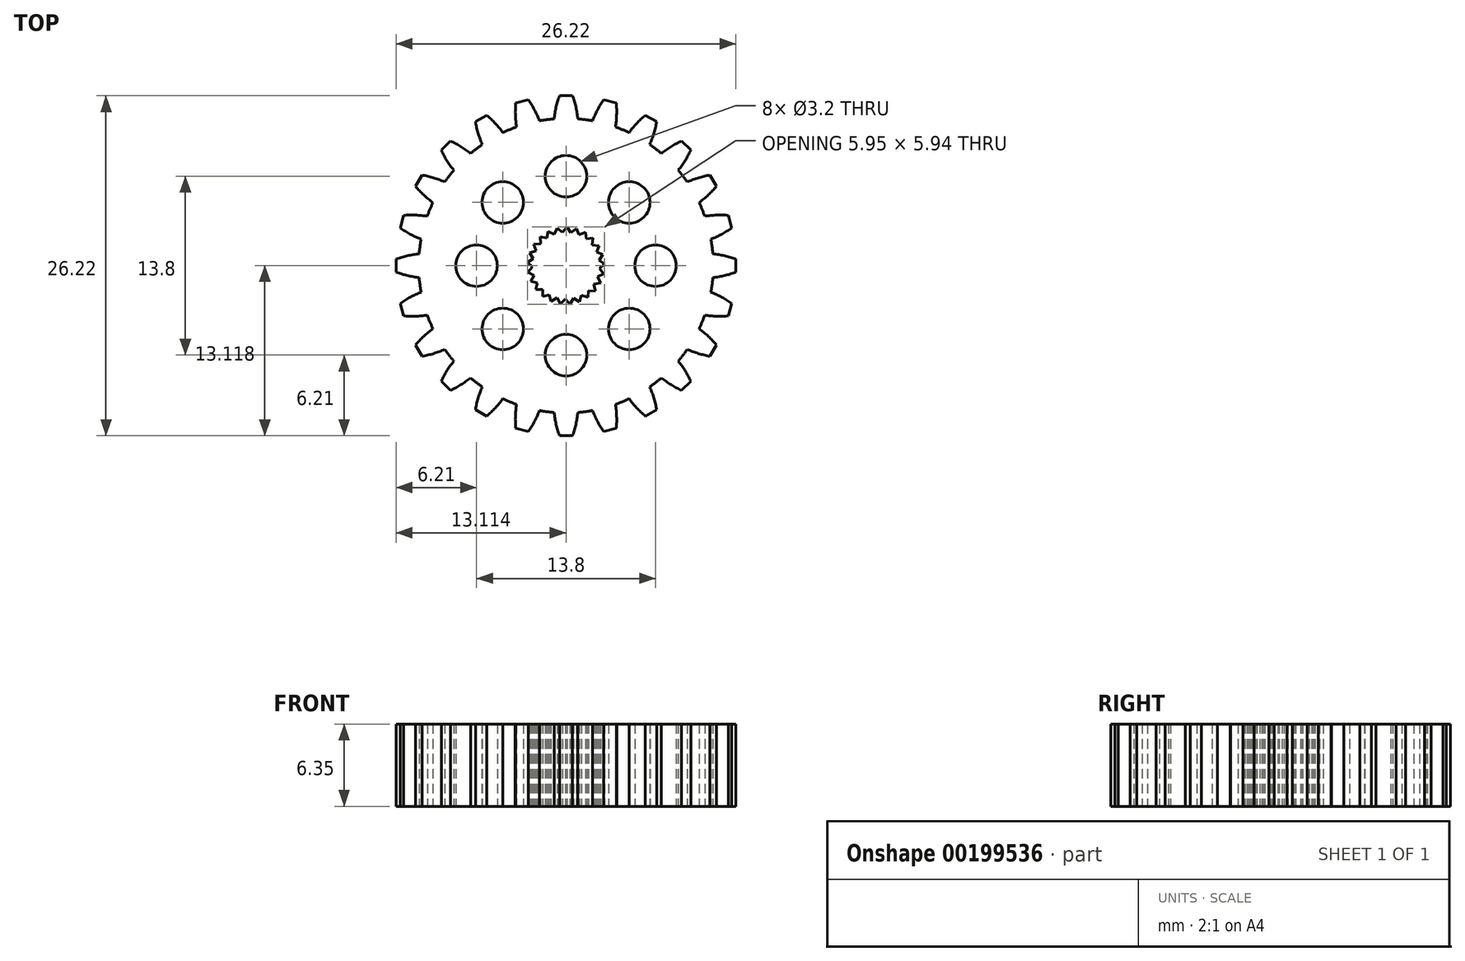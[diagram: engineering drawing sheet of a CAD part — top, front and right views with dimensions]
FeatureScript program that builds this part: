
annotation { "Feature Type Name" : "Feature", "Feature Type Description" : "" }
export const myFeature = defineFeature(function(context is Context, id is Id, definition is map)
    precondition{}
    {
        {
            var Q0;
            Q0=qCreatedBy(makeId("Top.planeOp"),FACE);
            var sketch = newSketch(context, id + "F0", { "sketchPlane" : qUnion([Q0])});
            skLineSegment(sketch, "E0", {"start": v(-0.5, 13.1) * mm, "end": v(0.5, 13.1) * mm});
            skArc(sketch, "E1", {"start": v(-0.5, 13.1) * mm, "mid": v(-0.76, 12.23) * mm, "end": v(-0.91, 11.32) * mm});
            skArc(sketch, "E2.MirrorCS", {"start": v(0.5, 13.1) * mm, "mid": v(0.76, 12.23) * mm, "end": v(0.91, 11.32) * mm});
            skPoint(sketch, "E3.center", {"position": v(0, 0) * mm});
            skLineSegment(sketch, "E4", {"start": v(-2.48, 1.65) * mm, "end": v(-2.31, 1.15) * mm});
            skLineSegment(sketch, "E5", {"start": v(-2.31, 1.15) * mm, "end": v(-2.81, 0.98) * mm});
            skLineSegment(sketch, "E6.1.0", {"start": v(-2.81, 0.98) * mm, "end": v(-2.53, 0.54) * mm});
            skLineSegment(sketch, "E6.1.1", {"start": v(-2.53, 0.54) * mm, "end": v(-2.97, 0.25) * mm});
            skLineSegment(sketch, "E6.2.0", {"start": v(-2.97, 0.25) * mm, "end": v(-2.58, -0.1) * mm});
            skLineSegment(sketch, "E6.2.1", {"start": v(-2.58, -0.1) * mm, "end": v(-2.94, -0.5) * mm});
            skLineSegment(sketch, "E6.3.0", {"start": v(-2.94, -0.5) * mm, "end": v(-2.47, -0.74) * mm});
            skLineSegment(sketch, "E6.3.1", {"start": v(-2.47, -0.74) * mm, "end": v(-2.72, -1.2) * mm});
            skLineSegment(sketch, "E6.4.0", {"start": v(-2.72, -1.2) * mm, "end": v(-2.21, -1.34) * mm});
            skLineSegment(sketch, "E6.4.1", {"start": v(-2.21, -1.34) * mm, "end": v(-2.34, -1.85) * mm});
            skLineSegment(sketch, "E6.5.0", {"start": v(-2.34, -1.85) * mm, "end": v(-1.8, -1.84) * mm});
            skLineSegment(sketch, "E6.5.1", {"start": v(-1.8, -1.84) * mm, "end": v(-1.8, -2.37) * mm});
            skLineSegment(sketch, "E6.6.0", {"start": v(-1.8, -2.37) * mm, "end": v(-1.3, -2.24) * mm});
            skLineSegment(sketch, "E6.6.1", {"start": v(-1.3, -2.24) * mm, "end": v(-1.16, -2.75) * mm});
            skLineSegment(sketch, "E6.7.0", {"start": v(-1.16, -2.75) * mm, "end": v(-0.7, -2.49) * mm});
            skLineSegment(sketch, "E6.7.1", {"start": v(-0.7, -2.49) * mm, "end": v(-0.44, -2.95) * mm});
            skLineSegment(sketch, "E6.8.0", {"start": v(-0.44, -2.95) * mm, "end": v(-0.06, -2.58) * mm});
            skLineSegment(sketch, "E6.8.1", {"start": v(-0.06, -2.58) * mm, "end": v(0.3, -2.96) * mm});
            skLineSegment(sketch, "E6.9.0", {"start": v(0.3, -2.96) * mm, "end": v(0.59, -2.52) * mm});
            skLineSegment(sketch, "E6.9.1", {"start": v(0.59, -2.52) * mm, "end": v(1.04, -2.8) * mm});
            skLineSegment(sketch, "E6.10.0", {"start": v(1.04, -2.8) * mm, "end": v(1.2, -2.3) * mm});
            skLineSegment(sketch, "E6.10.1", {"start": v(1.2, -2.3) * mm, "end": v(1.7, -2.45) * mm});
            skLineSegment(sketch, "E6.11.0", {"start": v(1.7, -2.45) * mm, "end": v(1.73, -1.92) * mm});
            skLineSegment(sketch, "E6.11.1", {"start": v(1.73, -1.92) * mm, "end": v(2.25, -1.95) * mm});
            skLineSegment(sketch, "E6.12.0", {"start": v(2.25, -1.95) * mm, "end": v(2.15, -1.43) * mm});
            skLineSegment(sketch, "E6.12.1", {"start": v(2.15, -1.43) * mm, "end": v(2.67, -1.33) * mm});
            skLineSegment(sketch, "E6.13.0", {"start": v(2.67, -1.33) * mm, "end": v(2.44, -0.85) * mm});
            skLineSegment(sketch, "E6.13.1", {"start": v(2.44, -0.85) * mm, "end": v(2.91, -0.62) * mm});
            skLineSegment(sketch, "E6.14.0", {"start": v(2.91, -0.62) * mm, "end": v(2.57, -0.22) * mm});
            skLineSegment(sketch, "E6.14.1", {"start": v(2.57, -0.22) * mm, "end": v(2.98, 0.12) * mm});
            skLineSegment(sketch, "E6.15.0", {"start": v(2.98, 0.12) * mm, "end": v(2.55, 0.43) * mm});
            skLineSegment(sketch, "E6.15.1", {"start": v(2.55, 0.43) * mm, "end": v(2.85, 0.86) * mm});
            skLineSegment(sketch, "E6.16.0", {"start": v(2.85, 0.86) * mm, "end": v(2.36, 1.05) * mm});
            skLineSegment(sketch, "E6.16.1", {"start": v(2.36, 1.05) * mm, "end": v(2.55, 1.54) * mm});
            skLineSegment(sketch, "E6.17.0", {"start": v(2.55, 1.54) * mm, "end": v(2.03, 1.6) * mm});
            skLineSegment(sketch, "E6.17.1", {"start": v(2.03, 1.6) * mm, "end": v(2.09, 2.13) * mm});
            skLineSegment(sketch, "E6.18.0", {"start": v(2.09, 2.13) * mm, "end": v(1.56, 2.06) * mm});
            skLineSegment(sketch, "E6.18.1", {"start": v(1.56, 2.06) * mm, "end": v(1.5, 2.58) * mm});
            skLineSegment(sketch, "E6.19.0", {"start": v(1.5, 2.58) * mm, "end": v(1, 2.38) * mm});
            skLineSegment(sketch, "E6.19.1", {"start": v(1, 2.38) * mm, "end": v(0.8, 2.87) * mm});
            skLineSegment(sketch, "E6.20.0", {"start": v(0.8, 2.87) * mm, "end": v(0.38, 2.56) * mm});
            skLineSegment(sketch, "E6.20.1", {"start": v(0.38, 2.56) * mm, "end": v(0.07, 2.98) * mm});
            skLineSegment(sketch, "E6.21.0", {"start": v(0.07, 2.98) * mm, "end": v(-0.27, 2.57) * mm});
            skLineSegment(sketch, "E6.21.1", {"start": v(-0.27, 2.57) * mm, "end": v(-0.68, 2.9) * mm});
            skLineSegment(sketch, "E6.22.0", {"start": v(-0.68, 2.9) * mm, "end": v(-0.9, 2.42) * mm});
            skLineSegment(sketch, "E6.22.1", {"start": v(-0.9, 2.42) * mm, "end": v(-1.38, 2.64) * mm});
            skLineSegment(sketch, "E6.23.0", {"start": v(-1.38, 2.64) * mm, "end": v(-1.47, 2.12) * mm});
            skLineSegment(sketch, "E6.23.1", {"start": v(-1.47, 2.12) * mm, "end": v(-2, 2.22) * mm});
            skLineSegment(sketch, "E6.24.0", {"start": v(-2, 2.22) * mm, "end": v(-1.95, 1.69) * mm});
            skLineSegment(sketch, "E6.24.1", {"start": v(-1.95, 1.69) * mm, "end": v(-2.48, 1.65) * mm});
            skCircle(sketch, "E7", {"center": v(0, 6.9) * mm, "radius": 1.6 * mm});
            skCircle(sketch, "E8.1.0", {"center": v(-4.88, 4.88) * mm, "radius": 1.6 * mm});
            skCircle(sketch, "E8.2.0", {"center": v(-6.9, 0) * mm, "radius": 1.6 * mm});
            skCircle(sketch, "E8.3.0", {"center": v(-4.88, -4.88) * mm, "radius": 1.6 * mm});
            skCircle(sketch, "E8.4.0", {"center": v(0, -6.9) * mm, "radius": 1.6 * mm});
            skCircle(sketch, "E8.5.0", {"center": v(4.88, -4.88) * mm, "radius": 1.6 * mm});
            skCircle(sketch, "E8.6.0", {"center": v(6.9, 0) * mm, "radius": 1.6 * mm});
            skCircle(sketch, "E8.7.0", {"center": v(4.88, 4.88) * mm, "radius": 1.6 * mm});
            skPoint(sketch, "E9.1.4", {"position": v(-0.5, 13.1) * mm});
            skArc(sketch, "E10", {"start": v(2.05, 11.18) * mm, "mid": v(1.48, 11.26) * mm, "end": v(0.91, 11.32) * mm});
            skPoint(sketch, "E11.orphan", {"position": v(2.9, 12.8) * mm});
            skPoint(sketch, "E12.orphan", {"position": v(0.94, 11) * mm});
            skPoint(sketch, "E13.orphan", {"position": v(-0.94, 11) * mm});
            skPoint(sketch, "E14.orphan", {"position": v(-2.9, 12.8) * mm});
            skArc(sketch, "E15.1.0", {"start": v(-0.91, 11.32) * mm, "mid": v(-1.48, 11.26) * mm, "end": v(-2.05, 11.18) * mm});
            skPoint(sketch, "E15.1.1", {"position": v(-3.88, 12.53) * mm});
            skArc(sketch, "E15.1.2", {"start": v(-3.88, 12.53) * mm, "mid": v(-3.9, 11.61) * mm, "end": v(-3.81, 10.7) * mm});
            skPoint(sketch, "E15.1.3", {"position": v(-3.75, 10.38) * mm});
            skArc(sketch, "E15.1.5", {"start": v(-2.9, 12.8) * mm, "mid": v(-2.43, 12.01) * mm, "end": v(-2.05, 11.18) * mm});
            skLineSegment(sketch, "E15.1.6", {"start": v(-3.88, 12.53) * mm, "end": v(-2.9, 12.8) * mm});
            skPoint(sketch, "E15.1.7", {"position": v(-1.94, 10.87) * mm});
            skArc(sketch, "E15.2.0", {"start": v(-3.81, 10.7) * mm, "mid": v(-4.35, 10.5) * mm, "end": v(-4.87, 10.26) * mm});
            skPoint(sketch, "E15.2.1", {"position": v(-6.99, 11.1) * mm});
            skArc(sketch, "E15.2.2", {"start": v(-6.99, 11.1) * mm, "mid": v(-6.78, 10.2) * mm, "end": v(-6.45, 9.35) * mm});
            skPoint(sketch, "E15.2.3", {"position": v(-6.31, 9.06) * mm});
            skPoint(sketch, "E15.2.4", {"position": v(-3.88, 12.53) * mm});
            skArc(sketch, "E15.2.5", {"start": v(-6.12, 11.6) * mm, "mid": v(-5.45, 10.97) * mm, "end": v(-4.87, 10.26) * mm});
            skLineSegment(sketch, "E15.2.6", {"start": v(-6.99, 11.1) * mm, "end": v(-6.12, 11.6) * mm});
            skPoint(sketch, "E15.2.7", {"position": v(-4.69, 10) * mm});
            skArc(sketch, "E15.3.0", {"start": v(-6.45, 9.35) * mm, "mid": v(-6.92, 9.01) * mm, "end": v(-7.36, 8.65) * mm});
            skPoint(sketch, "E15.3.1", {"position": v(-9.62, 8.91) * mm});
            skArc(sketch, "E15.3.2", {"start": v(-9.62, 8.91) * mm, "mid": v(-9.19, 8.1) * mm, "end": v(-8.65, 7.36) * mm});
            skPoint(sketch, "E15.3.3", {"position": v(-8.44, 7.11) * mm});
            skPoint(sketch, "E15.3.4", {"position": v(-6.99, 11.1) * mm});
            skArc(sketch, "E15.3.5", {"start": v(-8.91, 9.62) * mm, "mid": v(-8.1, 9.19) * mm, "end": v(-7.36, 8.65) * mm});
            skLineSegment(sketch, "E15.3.6", {"start": v(-9.62, 8.91) * mm, "end": v(-8.91, 9.62) * mm});
            skPoint(sketch, "E15.3.7", {"position": v(-7.11, 8.44) * mm});
            skArc(sketch, "E15.4.0", {"start": v(-8.65, 7.36) * mm, "mid": v(-9.01, 6.92) * mm, "end": v(-9.35, 6.45) * mm});
            skPoint(sketch, "E15.4.1", {"position": v(-11.6, 6.12) * mm});
            skArc(sketch, "E15.4.2", {"start": v(-11.6, 6.12) * mm, "mid": v(-10.97, 5.45) * mm, "end": v(-10.26, 4.87) * mm});
            skPoint(sketch, "E15.4.3", {"position": v(-10, 4.69) * mm});
            skPoint(sketch, "E15.4.4", {"position": v(-9.62, 8.91) * mm});
            skArc(sketch, "E15.4.5", {"start": v(-11.1, 6.99) * mm, "mid": v(-10.2, 6.78) * mm, "end": v(-9.35, 6.45) * mm});
            skLineSegment(sketch, "E15.4.6", {"start": v(-11.6, 6.12) * mm, "end": v(-11.1, 6.99) * mm});
            skPoint(sketch, "E15.4.7", {"position": v(-9.06, 6.31) * mm});
            skArc(sketch, "E15.5.0", {"start": v(-10.26, 4.87) * mm, "mid": v(-10.5, 4.35) * mm, "end": v(-10.7, 3.81) * mm});
            skPoint(sketch, "E15.5.1", {"position": v(-12.8, 2.9) * mm});
            skArc(sketch, "E15.5.2", {"start": v(-12.8, 2.9) * mm, "mid": v(-12.01, 2.43) * mm, "end": v(-11.18, 2.05) * mm});
            skPoint(sketch, "E15.5.3", {"position": v(-10.87, 1.94) * mm});
            skPoint(sketch, "E15.5.4", {"position": v(-11.6, 6.12) * mm});
            skArc(sketch, "E15.5.5", {"start": v(-12.53, 3.88) * mm, "mid": v(-11.61, 3.9) * mm, "end": v(-10.7, 3.81) * mm});
            skLineSegment(sketch, "E15.5.6", {"start": v(-12.8, 2.9) * mm, "end": v(-12.53, 3.88) * mm});
            skPoint(sketch, "E15.5.7", {"position": v(-10.38, 3.75) * mm});
            skArc(sketch, "E15.6.0", {"start": v(-11.18, 2.05) * mm, "mid": v(-11.26, 1.48) * mm, "end": v(-11.32, 0.91) * mm});
            skPoint(sketch, "E15.6.1", {"position": v(-13.1, -0.5) * mm});
            skArc(sketch, "E15.6.2", {"start": v(-13.1, -0.5) * mm, "mid": v(-12.23, -0.76) * mm, "end": v(-11.32, -0.91) * mm});
            skPoint(sketch, "E15.6.3", {"position": v(-11, -0.94) * mm});
            skPoint(sketch, "E15.6.4", {"position": v(-12.8, 2.9) * mm});
            skArc(sketch, "E15.6.5", {"start": v(-13.1, 0.5) * mm, "mid": v(-12.23, 0.76) * mm, "end": v(-11.32, 0.91) * mm});
            skLineSegment(sketch, "E15.6.6", {"start": v(-13.1, -0.5) * mm, "end": v(-13.1, 0.5) * mm});
            skPoint(sketch, "E15.6.7", {"position": v(-11, 0.94) * mm});
            skArc(sketch, "E15.7.0", {"start": v(-11.32, -0.91) * mm, "mid": v(-11.26, -1.48) * mm, "end": v(-11.18, -2.05) * mm});
            skPoint(sketch, "E15.7.1", {"position": v(-12.53, -3.88) * mm});
            skArc(sketch, "E15.7.2", {"start": v(-12.53, -3.88) * mm, "mid": v(-11.61, -3.9) * mm, "end": v(-10.7, -3.81) * mm});
            skPoint(sketch, "E15.7.3", {"position": v(-10.38, -3.75) * mm});
            skPoint(sketch, "E15.7.4", {"position": v(-13.1, -0.5) * mm});
            skArc(sketch, "E15.7.5", {"start": v(-12.8, -2.9) * mm, "mid": v(-12.01, -2.43) * mm, "end": v(-11.18, -2.05) * mm});
            skLineSegment(sketch, "E15.7.6", {"start": v(-12.53, -3.88) * mm, "end": v(-12.8, -2.9) * mm});
            skPoint(sketch, "E15.7.7", {"position": v(-10.87, -1.94) * mm});
            skArc(sketch, "E15.8.0", {"start": v(-10.7, -3.81) * mm, "mid": v(-10.5, -4.35) * mm, "end": v(-10.26, -4.87) * mm});
            skPoint(sketch, "E15.8.1", {"position": v(-11.1, -6.99) * mm});
            skArc(sketch, "E15.8.2", {"start": v(-11.1, -6.99) * mm, "mid": v(-10.2, -6.78) * mm, "end": v(-9.35, -6.45) * mm});
            skPoint(sketch, "E15.8.3", {"position": v(-9.06, -6.31) * mm});
            skPoint(sketch, "E15.8.4", {"position": v(-12.53, -3.88) * mm});
            skArc(sketch, "E15.8.5", {"start": v(-11.6, -6.12) * mm, "mid": v(-10.97, -5.45) * mm, "end": v(-10.26, -4.87) * mm});
            skLineSegment(sketch, "E15.8.6", {"start": v(-11.1, -6.99) * mm, "end": v(-11.6, -6.12) * mm});
            skPoint(sketch, "E15.8.7", {"position": v(-10, -4.69) * mm});
            skArc(sketch, "E15.9.0", {"start": v(-9.35, -6.45) * mm, "mid": v(-9.01, -6.92) * mm, "end": v(-8.65, -7.36) * mm});
            skPoint(sketch, "E15.9.1", {"position": v(-8.91, -9.62) * mm});
            skArc(sketch, "E15.9.2", {"start": v(-8.91, -9.62) * mm, "mid": v(-8.1, -9.19) * mm, "end": v(-7.36, -8.65) * mm});
            skPoint(sketch, "E15.9.3", {"position": v(-7.11, -8.44) * mm});
            skPoint(sketch, "E15.9.4", {"position": v(-11.1, -6.99) * mm});
            skArc(sketch, "E15.9.5", {"start": v(-9.62, -8.91) * mm, "mid": v(-9.19, -8.1) * mm, "end": v(-8.65, -7.36) * mm});
            skLineSegment(sketch, "E15.9.6", {"start": v(-8.91, -9.62) * mm, "end": v(-9.62, -8.91) * mm});
            skPoint(sketch, "E15.9.7", {"position": v(-8.44, -7.11) * mm});
            skArc(sketch, "E15.10.0", {"start": v(-7.36, -8.65) * mm, "mid": v(-6.92, -9.01) * mm, "end": v(-6.45, -9.35) * mm});
            skPoint(sketch, "E15.10.1", {"position": v(-6.12, -11.6) * mm});
            skArc(sketch, "E15.10.2", {"start": v(-6.12, -11.6) * mm, "mid": v(-5.45, -10.97) * mm, "end": v(-4.87, -10.26) * mm});
            skPoint(sketch, "E15.10.3", {"position": v(-4.69, -10) * mm});
            skPoint(sketch, "E15.10.4", {"position": v(-8.91, -9.62) * mm});
            skArc(sketch, "E15.10.5", {"start": v(-6.99, -11.1) * mm, "mid": v(-6.78, -10.2) * mm, "end": v(-6.45, -9.35) * mm});
            skLineSegment(sketch, "E15.10.6", {"start": v(-6.12, -11.6) * mm, "end": v(-6.99, -11.1) * mm});
            skPoint(sketch, "E15.10.7", {"position": v(-6.31, -9.06) * mm});
            skArc(sketch, "E15.11.0", {"start": v(-4.87, -10.26) * mm, "mid": v(-4.35, -10.5) * mm, "end": v(-3.81, -10.7) * mm});
            skPoint(sketch, "E15.11.1", {"position": v(-2.9, -12.8) * mm});
            skArc(sketch, "E15.11.2", {"start": v(-2.9, -12.8) * mm, "mid": v(-2.43, -12.01) * mm, "end": v(-2.05, -11.18) * mm});
            skPoint(sketch, "E15.11.3", {"position": v(-1.94, -10.87) * mm});
            skPoint(sketch, "E15.11.4", {"position": v(-6.12, -11.6) * mm});
            skArc(sketch, "E15.11.5", {"start": v(-3.88, -12.53) * mm, "mid": v(-3.9, -11.61) * mm, "end": v(-3.81, -10.7) * mm});
            skLineSegment(sketch, "E15.11.6", {"start": v(-2.9, -12.8) * mm, "end": v(-3.88, -12.53) * mm});
            skPoint(sketch, "E15.11.7", {"position": v(-3.75, -10.38) * mm});
            skArc(sketch, "E15.12.0", {"start": v(-2.05, -11.18) * mm, "mid": v(-1.48, -11.26) * mm, "end": v(-0.91, -11.32) * mm});
            skPoint(sketch, "E15.12.1", {"position": v(0.5, -13.1) * mm});
            skArc(sketch, "E15.12.2", {"start": v(0.5, -13.1) * mm, "mid": v(0.76, -12.23) * mm, "end": v(0.91, -11.32) * mm});
            skPoint(sketch, "E15.12.3", {"position": v(0.94, -11) * mm});
            skPoint(sketch, "E15.12.4", {"position": v(-2.9, -12.8) * mm});
            skArc(sketch, "E15.12.5", {"start": v(-0.5, -13.1) * mm, "mid": v(-0.76, -12.23) * mm, "end": v(-0.91, -11.32) * mm});
            skLineSegment(sketch, "E15.12.6", {"start": v(0.5, -13.1) * mm, "end": v(-0.5, -13.1) * mm});
            skPoint(sketch, "E15.12.7", {"position": v(-0.94, -11) * mm});
            skArc(sketch, "E15.13.0", {"start": v(0.91, -11.32) * mm, "mid": v(1.48, -11.26) * mm, "end": v(2.05, -11.18) * mm});
            skPoint(sketch, "E15.13.1", {"position": v(3.88, -12.53) * mm});
            skArc(sketch, "E15.13.2", {"start": v(3.88, -12.53) * mm, "mid": v(3.9, -11.61) * mm, "end": v(3.81, -10.7) * mm});
            skPoint(sketch, "E15.13.3", {"position": v(3.75, -10.38) * mm});
            skPoint(sketch, "E15.13.4", {"position": v(0.5, -13.1) * mm});
            skArc(sketch, "E15.13.5", {"start": v(2.9, -12.8) * mm, "mid": v(2.43, -12.01) * mm, "end": v(2.05, -11.18) * mm});
            skLineSegment(sketch, "E15.13.6", {"start": v(3.88, -12.53) * mm, "end": v(2.9, -12.8) * mm});
            skPoint(sketch, "E15.13.7", {"position": v(1.94, -10.87) * mm});
            skArc(sketch, "E15.14.0", {"start": v(3.81, -10.7) * mm, "mid": v(4.35, -10.5) * mm, "end": v(4.87, -10.26) * mm});
            skPoint(sketch, "E15.14.1", {"position": v(6.99, -11.1) * mm});
            skArc(sketch, "E15.14.2", {"start": v(6.99, -11.1) * mm, "mid": v(6.78, -10.2) * mm, "end": v(6.45, -9.35) * mm});
            skPoint(sketch, "E15.14.3", {"position": v(6.31, -9.06) * mm});
            skPoint(sketch, "E15.14.4", {"position": v(3.88, -12.53) * mm});
            skArc(sketch, "E15.14.5", {"start": v(6.12, -11.6) * mm, "mid": v(5.45, -10.97) * mm, "end": v(4.87, -10.26) * mm});
            skLineSegment(sketch, "E15.14.6", {"start": v(6.99, -11.1) * mm, "end": v(6.12, -11.6) * mm});
            skPoint(sketch, "E15.14.7", {"position": v(4.69, -10) * mm});
            skArc(sketch, "E15.15.0", {"start": v(6.45, -9.35) * mm, "mid": v(6.92, -9.01) * mm, "end": v(7.36, -8.65) * mm});
            skPoint(sketch, "E15.15.1", {"position": v(9.62, -8.91) * mm});
            skArc(sketch, "E15.15.2", {"start": v(9.62, -8.91) * mm, "mid": v(9.19, -8.1) * mm, "end": v(8.65, -7.36) * mm});
            skPoint(sketch, "E15.15.3", {"position": v(8.44, -7.11) * mm});
            skPoint(sketch, "E15.15.4", {"position": v(6.99, -11.1) * mm});
            skArc(sketch, "E15.15.5", {"start": v(8.91, -9.62) * mm, "mid": v(8.1, -9.19) * mm, "end": v(7.36, -8.65) * mm});
            skLineSegment(sketch, "E15.15.6", {"start": v(9.62, -8.91) * mm, "end": v(8.91, -9.62) * mm});
            skPoint(sketch, "E15.15.7", {"position": v(7.11, -8.44) * mm});
            skArc(sketch, "E15.16.0", {"start": v(8.65, -7.36) * mm, "mid": v(9.01, -6.92) * mm, "end": v(9.35, -6.45) * mm});
            skPoint(sketch, "E15.16.1", {"position": v(11.6, -6.12) * mm});
            skArc(sketch, "E15.16.2", {"start": v(11.6, -6.12) * mm, "mid": v(10.97, -5.45) * mm, "end": v(10.26, -4.87) * mm});
            skPoint(sketch, "E15.16.3", {"position": v(10, -4.69) * mm});
            skPoint(sketch, "E15.16.4", {"position": v(9.62, -8.91) * mm});
            skArc(sketch, "E15.16.5", {"start": v(11.1, -6.99) * mm, "mid": v(10.2, -6.78) * mm, "end": v(9.35, -6.45) * mm});
            skLineSegment(sketch, "E15.16.6", {"start": v(11.6, -6.12) * mm, "end": v(11.1, -6.99) * mm});
            skPoint(sketch, "E15.16.7", {"position": v(9.06, -6.31) * mm});
            skArc(sketch, "E15.17.0", {"start": v(10.26, -4.87) * mm, "mid": v(10.5, -4.35) * mm, "end": v(10.7, -3.81) * mm});
            skPoint(sketch, "E15.17.1", {"position": v(12.8, -2.9) * mm});
            skArc(sketch, "E15.17.2", {"start": v(12.8, -2.9) * mm, "mid": v(12.01, -2.43) * mm, "end": v(11.18, -2.05) * mm});
            skPoint(sketch, "E15.17.3", {"position": v(10.87, -1.94) * mm});
            skPoint(sketch, "E15.17.4", {"position": v(11.6, -6.12) * mm});
            skArc(sketch, "E15.17.5", {"start": v(12.53, -3.88) * mm, "mid": v(11.61, -3.9) * mm, "end": v(10.7, -3.81) * mm});
            skLineSegment(sketch, "E15.17.6", {"start": v(12.8, -2.9) * mm, "end": v(12.53, -3.88) * mm});
            skPoint(sketch, "E15.17.7", {"position": v(10.38, -3.75) * mm});
            skArc(sketch, "E15.18.0", {"start": v(11.18, -2.05) * mm, "mid": v(11.26, -1.48) * mm, "end": v(11.32, -0.91) * mm});
            skPoint(sketch, "E15.18.1", {"position": v(13.1, 0.5) * mm});
            skArc(sketch, "E15.18.2", {"start": v(13.1, 0.5) * mm, "mid": v(12.23, 0.76) * mm, "end": v(11.32, 0.91) * mm});
            skPoint(sketch, "E15.18.3", {"position": v(11, 0.94) * mm});
            skPoint(sketch, "E15.18.4", {"position": v(12.8, -2.9) * mm});
            skArc(sketch, "E15.18.5", {"start": v(13.1, -0.5) * mm, "mid": v(12.23, -0.76) * mm, "end": v(11.32, -0.91) * mm});
            skLineSegment(sketch, "E15.18.6", {"start": v(13.1, 0.5) * mm, "end": v(13.1, -0.5) * mm});
            skPoint(sketch, "E15.18.7", {"position": v(11, -0.94) * mm});
            skArc(sketch, "E15.19.0", {"start": v(11.32, 0.91) * mm, "mid": v(11.26, 1.48) * mm, "end": v(11.18, 2.05) * mm});
            skPoint(sketch, "E15.19.1", {"position": v(12.53, 3.88) * mm});
            skArc(sketch, "E15.19.2", {"start": v(12.53, 3.88) * mm, "mid": v(11.61, 3.9) * mm, "end": v(10.7, 3.81) * mm});
            skPoint(sketch, "E15.19.3", {"position": v(10.38, 3.75) * mm});
            skPoint(sketch, "E15.19.4", {"position": v(13.1, 0.5) * mm});
            skArc(sketch, "E15.19.5", {"start": v(12.8, 2.9) * mm, "mid": v(12.01, 2.43) * mm, "end": v(11.18, 2.05) * mm});
            skLineSegment(sketch, "E15.19.6", {"start": v(12.53, 3.88) * mm, "end": v(12.8, 2.9) * mm});
            skPoint(sketch, "E15.19.7", {"position": v(10.87, 1.94) * mm});
            skArc(sketch, "E15.20.0", {"start": v(10.7, 3.81) * mm, "mid": v(10.5, 4.35) * mm, "end": v(10.26, 4.87) * mm});
            skPoint(sketch, "E15.20.1", {"position": v(11.1, 6.99) * mm});
            skArc(sketch, "E15.20.2", {"start": v(11.1, 6.99) * mm, "mid": v(10.2, 6.78) * mm, "end": v(9.35, 6.45) * mm});
            skPoint(sketch, "E15.20.3", {"position": v(9.06, 6.31) * mm});
            skPoint(sketch, "E15.20.4", {"position": v(12.53, 3.88) * mm});
            skArc(sketch, "E15.20.5", {"start": v(11.6, 6.12) * mm, "mid": v(10.97, 5.45) * mm, "end": v(10.26, 4.87) * mm});
            skLineSegment(sketch, "E15.20.6", {"start": v(11.1, 6.99) * mm, "end": v(11.6, 6.12) * mm});
            skPoint(sketch, "E15.20.7", {"position": v(10, 4.69) * mm});
            skArc(sketch, "E15.21.0", {"start": v(9.35, 6.45) * mm, "mid": v(9.01, 6.92) * mm, "end": v(8.65, 7.36) * mm});
            skPoint(sketch, "E15.21.1", {"position": v(8.91, 9.62) * mm});
            skArc(sketch, "E15.21.2", {"start": v(8.91, 9.62) * mm, "mid": v(8.1, 9.19) * mm, "end": v(7.36, 8.65) * mm});
            skPoint(sketch, "E15.21.3", {"position": v(7.11, 8.44) * mm});
            skPoint(sketch, "E15.21.4", {"position": v(11.1, 6.99) * mm});
            skArc(sketch, "E15.21.5", {"start": v(9.62, 8.91) * mm, "mid": v(9.19, 8.1) * mm, "end": v(8.65, 7.36) * mm});
            skLineSegment(sketch, "E15.21.6", {"start": v(8.91, 9.62) * mm, "end": v(9.62, 8.91) * mm});
            skPoint(sketch, "E15.21.7", {"position": v(8.44, 7.11) * mm});
            skArc(sketch, "E15.22.0", {"start": v(7.36, 8.65) * mm, "mid": v(6.92, 9.01) * mm, "end": v(6.45, 9.35) * mm});
            skPoint(sketch, "E15.22.1", {"position": v(6.12, 11.6) * mm});
            skArc(sketch, "E15.22.2", {"start": v(6.12, 11.6) * mm, "mid": v(5.45, 10.97) * mm, "end": v(4.87, 10.26) * mm});
            skPoint(sketch, "E15.22.3", {"position": v(4.69, 10) * mm});
            skPoint(sketch, "E15.22.4", {"position": v(8.91, 9.62) * mm});
            skArc(sketch, "E15.22.5", {"start": v(6.99, 11.1) * mm, "mid": v(6.78, 10.2) * mm, "end": v(6.45, 9.35) * mm});
            skLineSegment(sketch, "E15.22.6", {"start": v(6.12, 11.6) * mm, "end": v(6.99, 11.1) * mm});
            skPoint(sketch, "E15.22.7", {"position": v(6.31, 9.06) * mm});
            skArc(sketch, "E15.23.0", {"start": v(4.87, 10.26) * mm, "mid": v(4.35, 10.5) * mm, "end": v(3.81, 10.7) * mm});
            skArc(sketch, "E15.23.2", {"start": v(2.9, 12.8) * mm, "mid": v(2.43, 12.01) * mm, "end": v(2.05, 11.18) * mm});
            skPoint(sketch, "E15.23.3", {"position": v(1.94, 10.87) * mm});
            skPoint(sketch, "E15.23.4", {"position": v(6.12, 11.6) * mm});
            skArc(sketch, "E15.23.5", {"start": v(3.88, 12.53) * mm, "mid": v(3.9, 11.61) * mm, "end": v(3.81, 10.7) * mm});
            skLineSegment(sketch, "E15.23.6", {"start": v(2.9, 12.8) * mm, "end": v(3.88, 12.53) * mm});
            skPoint(sketch, "E15.23.7", {"position": v(3.75, 10.38) * mm});
            skSolve(sketch);
        }
        {
            var Q0;
            Q0 = qSketchRegion(id + "F0", true);
            extrude(context, id + "F1", {"entities" : qUnion([Q0]), "depth" : 6.35 * mm});
        }
    });
